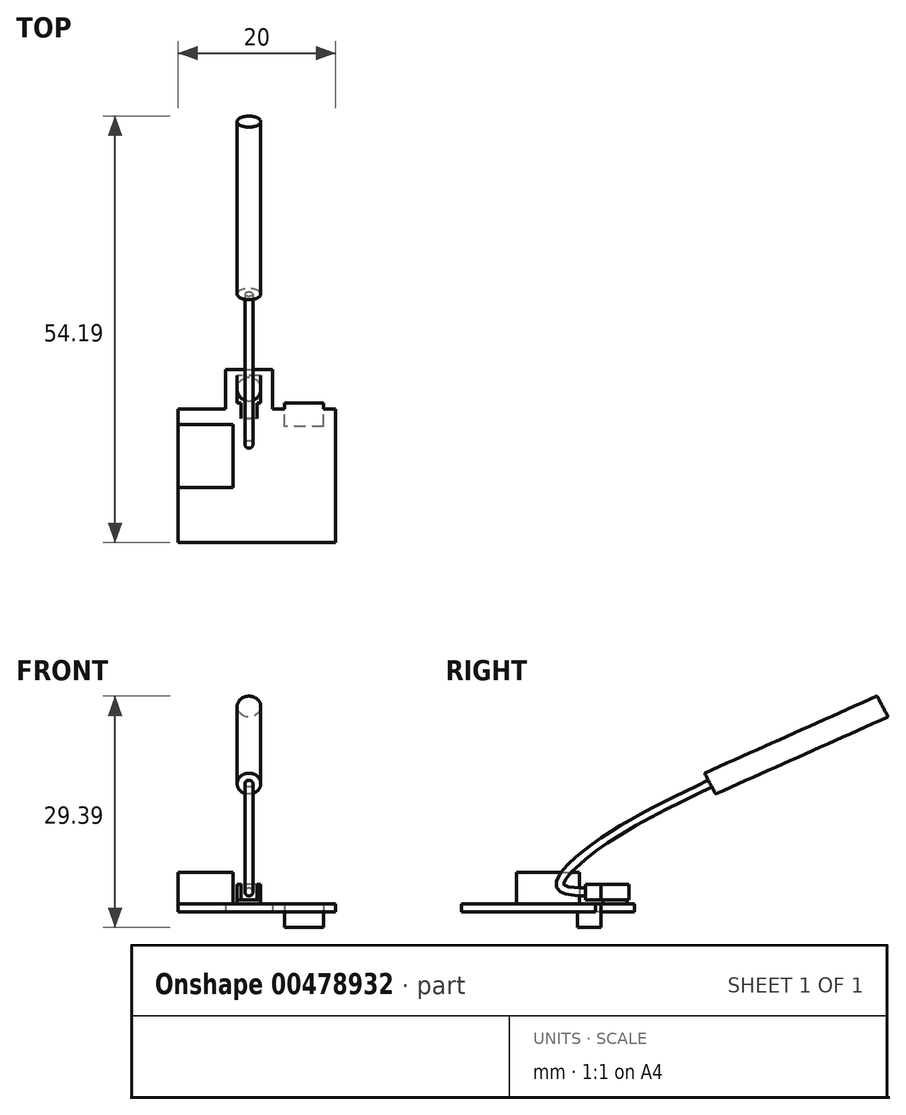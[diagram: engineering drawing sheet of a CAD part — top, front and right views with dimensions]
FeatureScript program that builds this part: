
annotation { "Feature Type Name" : "Feature", "Feature Type Description" : "" }
export const myFeature = defineFeature(function(context is Context, id is Id, definition is map)
    precondition{}
    {
        {
            var Q0;
            Q0=qCreatedBy(makeId("Top.planeOp"),FACE);
            var sketch = newSketch(context, id + "F0", { "sketchPlane" : qUnion([Q0])});
            skLineSegment(sketch, "E0.bottom", {"start": v(10, -8.5) * mm, "end": v(-10, -8.5) * mm});
            skLineSegment(sketch, "E0.top", {"start": v(10, 8.5) * mm, "end": v(-10, 8.5) * mm});
            skLineSegment(sketch, "E0.left", {"start": v(10, -8.5) * mm, "end": v(10, 8.5) * mm});
            skLineSegment(sketch, "E0.right", {"start": v(-10, -8.5) * mm, "end": v(-10, 8.5) * mm});
            skPoint(sketch, "E0.middle", {"position": v(0, 0) * mm});
            skLineSegment(sketch, "E1", {"start": v(-4, 13.5) * mm, "end": v(17.67, 13.5) * mm});
            skLineSegment(sketch, "E2", {"start": v(-4, 13.5) * mm, "end": v(-4, 8.5) * mm});
            skLineSegment(sketch, "E3", {"start": v(2, 13.5) * mm, "end": v(2, 8.5) * mm});
            skLineSegment(sketch, "E4.bottom", {"start": v(8.5, 6.25) * mm, "end": v(3.5, 6.25) * mm});
            skLineSegment(sketch, "E4.top", {"start": v(8.5, 9.25) * mm, "end": v(3.5, 9.25) * mm});
            skLineSegment(sketch, "E4.left", {"start": v(8.5, 6.25) * mm, "end": v(8.5, 9.25) * mm});
            skLineSegment(sketch, "E4.right", {"start": v(3.5, 6.25) * mm, "end": v(3.5, 9.25) * mm});
            skPoint(sketch, "E4.middle", {"position": v(6, 7.75) * mm});
            skLineSegment(sketch, "E5.bottom", {"start": v(-3, -1.5) * mm, "end": v(-10, -1.5) * mm});
            skLineSegment(sketch, "E5.top", {"start": v(-3, 6.5) * mm, "end": v(-10, 6.5) * mm});
            skLineSegment(sketch, "E5.left", {"start": v(-3, -1.5) * mm, "end": v(-3, 6.5) * mm});
            skLineSegment(sketch, "E5.right", {"start": v(-10, -1.5) * mm, "end": v(-10, 6.5) * mm});
            skPoint(sketch, "E5.middle", {"position": v(-6.5, 2.5) * mm});
            skCircle(sketch, "E6", {"center": v(-1, 11) * mm, "radius": 1.5 * mm});
            skSolve(sketch);
        }
        {
            var Q0;
            Q0 = qSketchRegion(id + "F0", true);
            var Q1;
            Q1=makeQuery(id+"F0.imprint","IMPRINT",FACE,{"disambiguationData":[TD([[makeQuery(id+"F0.imprint","IMPRINT",EDGE,{"derivedFrom":sQuery(id+"F0.wireOp",EDGE,"E6")}),1.0]])]});
            extrude(context, id + "F1", {"entities" : qUnion([Q0, Q1]), "endBound" : BoundingType.SYMMETRIC, "depth" : 1 * mm, "offsetDistance" : 25 * mm});
        }
        {
            var Q0;
            Q0=makeQuery(id+"F0.imprint","IMPRINT",FACE,{"disambiguationData":[TD([[makeQuery(id+"F0.imprint","IMPRINT",EDGE,{"derivedFrom":sQuery(id+"F0.wireOp",EDGE,"E6")}),1.0]])]});
            extrude(context, id + "F2", {"entities" : qUnion([Q0]), "operationType" : NewBodyOperationType.ADD, "depth" : 1 * mm, "offsetDistance" : 25 * mm});
        }
        {
            var Q0;
            {var subQ5=sQuery(id+"F0.wireOp",EDGE,"E4.bottom");Q0=makeQuery(id+"F0.imprint","IMPRINT",FACE,{"disambiguationData":[TD([[makeQuery(id+"F0.imprint","IMPRINT",EDGE,{"derivedFrom":subQ5}),-1.0]])]});}
            var Q1;
            {var subQ5=sQuery(id+"F0.wireOp",EDGE,"E4.top");Q1=makeQuery(id+"F0.imprint","IMPRINT",FACE,{"disambiguationData":[TD([[makeQuery(id+"F0.imprint","IMPRINT",EDGE,{"derivedFrom":subQ5}),1.0]])]});}
            extrude(context, id + "F3", {"entities" : qUnion([Q0, Q1]), "operationType" : NewBodyOperationType.ADD, "oppositeDirection" : true, "depth" : 2.5 * mm, "offsetDistance" : 25 * mm});
        }
        {
            var Q0;
            Q0=makeQuery(id+"F0.imprint","IMPRINT",FACE,{"disambiguationData":[TD([[makeQuery(id+"F0.imprint","IMPRINT",EDGE,{"derivedFrom":sQuery(id+"F0.wireOp",EDGE,"E5.bottom")}),-1.0]])]});
            extrude(context, id + "F4", {"entities" : qUnion([Q0]), "operationType" : NewBodyOperationType.ADD, "depth" : 4.5 * mm, "offsetDistance" : 25 * mm});
        }
        {
            var Q0;
            Q0=makeQuery(id+"F2.opExtrude","CAP_FACE",FACE,{"disambiguationData":[OSD([sQuery(id+"F0.wireOp",EDGE,"E6")])],"isStart":false});
            var sketch = newSketch(context, id + "F5", { "sketchPlane" : qUnion([Q0])});
            skLineSegment(sketch, "E7.bottom", {"start": v(0.5, 9.25) * mm, "end": v(0, 9.25) * mm});
            skLineSegment(sketch, "E7.top", {"start": v(0.5, 12.75) * mm, "end": v(-2.5, 12.75) * mm});
            skLineSegment(sketch, "E7.left", {"start": v(0.5, 9.25) * mm, "end": v(0.5, 12.75) * mm});
            skLineSegment(sketch, "E7.right", {"start": v(-2.5, 9.25) * mm, "end": v(-2.5, 12.75) * mm});
            skPoint(sketch, "E7.middle", {"position": v(-1, 11) * mm});
            skLineSegment(sketch, "E8.bottom", {"start": v(0, 7.25) * mm, "end": v(-2, 7.25) * mm});
            skLineSegment(sketch, "E8.left", {"start": v(0, 7.25) * mm, "end": v(0, 9.25) * mm});
            skLineSegment(sketch, "E8.right", {"start": v(-2, 7.25) * mm, "end": v(-2, 9.25) * mm});
            skPoint(sketch, "E8.top.start.orphan", {"position": v(0, 14.75) * mm});
            skPoint(sketch, "E9.trimOffspring.end.orphan", {"position": v(-2, 14.75) * mm});
            skLineSegment(sketch, "E10.trimOffspring", {"start": v(-2, 9.25) * mm, "end": v(-2.5, 9.25) * mm});
            skSolve(sketch);
        }
        {
            var Q0;
            Q0 = qSketchRegion(id + "F5", true);
            extrude(context, id + "F6", {"entities" : qUnion([Q0]), "operationType" : NewBodyOperationType.ADD, "depth" : 2 * mm, "offsetDistance" : 25 * mm});
        }
        {
            var Q0;
            Q0=makeQuery(id+"F6.opExtrude","SWEPT_FACE",FACE,{"disambiguationData":[OSD([sQuery(id+"F5.wireOp",EDGE,"E8.bottom")])]});
            var sketch = newSketch(context, id + "F7", { "sketchPlane" : qUnion([Q0])});
            skCircle(sketch, "E11", {"center": v(-1, 2) * mm, "radius": 0.5 * mm});
            skSolve(sketch);
        }
        {
            var Q0;
            Q0=qCreatedBy(makeId("Right.planeOp"),FACE);
            cPlane(context, id + "F8", {"entities" : qUnion([Q0]), "cplaneType" : CPlaneType.OFFSET, "offset" : 1 * mm, "oppositeDirection" : true, "width" : 150 * mm, "height" : 150 * mm});
        }
        {
            var Q0;
            Q0=qCreatedBy(id+"F8.planeOp",FACE);
            var sketch = newSketch(context, id + "F9", { "sketchPlane" : qUnion([Q0])});
            skFitSpline(sketch, "E12", {"points": [v(7.25, 2) * mm, v(4.03, 2.76) * mm, v(8.07, 7.46) * mm, v(23.07, 15.77) * mm], "startDerivative": vector(-20.64, 0.83) * mm, "endDerivative": vector(33.45, 16.11) * mm});
            skLineSegment(sketch, "E13", {"start": v(23.07, 15.77) * mm, "end": v(44.98, 25.57) * mm});
            skSolve(sketch);
        }
        {
            var Q0;
            Q0=makeQuery(id+"F7.imprint","IMPRINT",FACE,{"disambiguationData":[TD([[makeQuery(id+"F7.imprint","IMPRINT",EDGE,{"derivedFrom":sQuery(id+"F7.wireOp",EDGE,"E11")}),1.0]])]});
            var Q1;
            Q1=sQuery(id+"F9.wireOp",EDGE,"E12");
            sweep(context, id + "F10", {"operationType" : NewBodyOperationType.ADD, "profiles" : qUnion([Q0]), "path" : qUnion([Q1])});
        }
        {
            var Q0;
            Q0=makeQuery(id+"F10.opSweep","CAP_FACE",FACE,{"disambiguationData":[OSD([sQuery(id+"F7.wireOp",EDGE,"E11"),sQuery(id+"F9.wireOp",VERTEX,"E12.end")])],"isStart":false});
            var sketch = newSketch(context, id + "F11", { "sketchPlane" : qUnion([Q0])});
            skCircle(sketch, "E14", {"center": v(1, 3.08) * mm, "radius": 1.5 * mm});
            skSolve(sketch);
        }
        {
            var Q0;
            Q0=makeQuery(id+"F11.imprint","IMPRINT",FACE,{"disambiguationData":[TD([[makeQuery(id+"F11.imprint","IMPRINT",EDGE,{"derivedFrom":sQuery(id+"F11.wireOp",EDGE,"E14")}),1.0]])]});
            var Q1;
            Q1=makeQuery(id+"F11.imprint","IMPRINT",FACE,{"disambiguationData":[TD([[makeQuery(id+"F11.imprint","IMPRINT",EDGE,{"derivedFrom":makeQuery(id+"F10.opSweep","CAP_EDGE",EDGE,{"disambiguationData":[OSD([sQuery(id+"F7.wireOp",EDGE,"E11"),sQuery(id+"F9.wireOp",VERTEX,"E12.end")])],"isStart":false})}),1.0]])]});
            var Q2;
            Q2=sQuery(id+"F9.wireOp",EDGE,"E13");
            sweep(context, id + "F12", {"profiles" : qUnion([Q0, Q1]), "path" : qUnion([Q2])});
        }
    });
